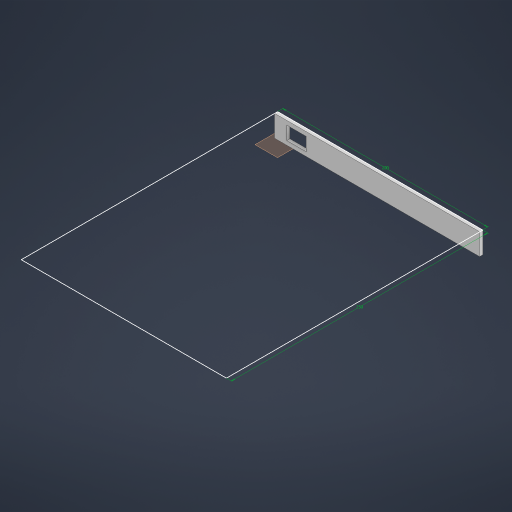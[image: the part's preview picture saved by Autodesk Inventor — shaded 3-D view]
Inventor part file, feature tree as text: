
AUTODESK INVENTOR PART (.ipt)
format: ipt  version: 2023 (Build 270158000, 158)  size: 238,592 bytes
history: native  units: mm
features: extrude x5, sketch x3, other x2, shell x1, plane x1
ambient origin geometry x8: Origin, YZ Plane, XZ Plane, XY Plane, X Axis, Y Axis, Z Axis, Center Point
bodies: Body1 (feature_tree)
feature tree (12):
  other  "block"
  extrude  "ext_block"  Depth=250.0mm
  shell  "Shell2"  Thickness=12.0mm
  extrude  "holes"  Depth=12.0mm
  extrude  "pwr_button_hole"  Depth=17.0mm
  plane  "Work Plane1"
  extrude  "back_cover_cut"  Depth=12.0mm
  extrude  "Extrusion8"  Depth=12.0mm
  other  "lines_base"
  sketch  "Sketch4"  dims[d0=200.0mm d1=250.0mm d2=12.0mm]
  sketch  "Sketch5"  dims[d3=12.0mm d4=25.0mm]
  sketch  "Sketch9"  dims[d5=17.0mm d6=17.0mm d7=25.0mm d8=75.0mm d9=80.0mm d10=65.0mm d11=60.0mm d12=6.0mm d13=84.0mm d14=90.0deg d15=25.0mm d16=125.0mm d17=70.0mm d19=14.0mm d20=10.0mm d22=10.0mm d24=5.0mm d25=10.0mm d26=65.0mm d27=95.0mm d31=200.0mm d32=250.0mm d35=24.0mm d36=0.0mm d37=3.0mm d38=24.0mm d39=0.0mm d40=19.0mm d41=13.0mm d42=4.0mm d43=12.0mm d44=24.0mm d45=0.0mm d49=0.0mm d50=0.0mm d62=0.0mm d63=0.0mm d33=0.5mm d34=0.872665mm d64=0.5mm d65=0.872665mm]
